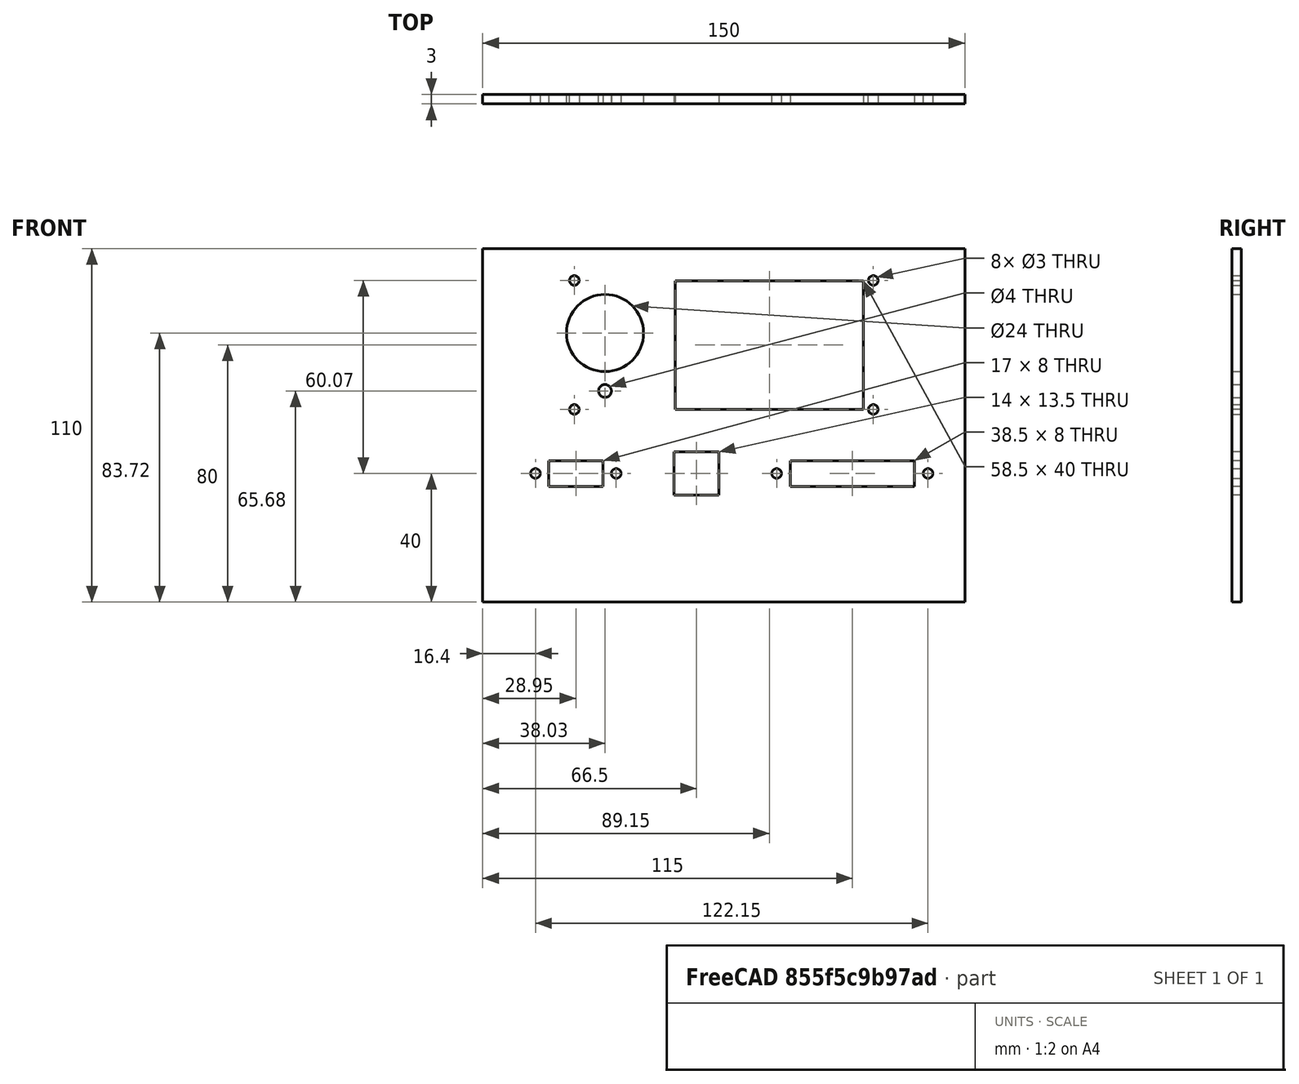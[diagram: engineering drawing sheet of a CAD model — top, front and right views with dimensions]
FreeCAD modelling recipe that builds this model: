
FCSTD DOCUMENT  (FreeCAD 0.19R24291 (Git))
Label: MountMini12864
License: All rights reserved
LicenseURL: http://en.wikipedia.org/wiki/All_rights_reserved
objects: TechDraw::DrawViewDimension×26, Sketcher::SketchObject×4, PartDesign::Pocket×2, PartDesign::Pad×1, Spreadsheet::Sheet×1, TechDraw::DrawSVGTemplate×1, PartDesign::Body×1, App::Part×1, TechDraw::DrawViewPart×1, TechDraw::DrawPage×1
note: 11 computed .brp shape members not serialized (recipe doc carries the construction recipe); baked Part::Feature solids carry a one-line shape summary decoded from their .brp

FEATURE [Sketcher::SketchObject] Sketch
  FullyConstrained = true
  MapMode = 5
  Placement = pos=(0,0,0) rot=(1,0,0;1.5708rad)
  Support = -> [XZ_Plane001]
  expr: Constraints[10] = <<Spreadsheet>>.Height
  expr: Constraints[9] = <<Spreadsheet>>.Width
  expr: Constraints[11] = <<Spreadsheet>>.OffsetVert
  expr: Constraints[12] = <<Spreadsheet>>.OffsetHorz
  sketch-geometry (5):
    g0: LineSegment StartX=-55 StartY=45 StartZ=0 EndX=95 EndY=45 EndZ=0
    g1: LineSegment StartX=95 StartY=45 StartZ=0 EndX=95 EndY=-65 EndZ=0
    g2: LineSegment StartX=95 StartY=-65 StartZ=0 EndX=-55 EndY=-65 EndZ=0
    g3: LineSegment StartX=-55 StartY=-65 StartZ=0 EndX=-55 EndY=45 EndZ=0
    g4: GeomPoint X=20 Y=-10 Z=0
  constraints (13):
    c: Coincident(g0,g1)
    c: Coincident(g1,g2)
    c: Coincident(g2,g3)
    c: Coincident(g3,g0)
    c: Horizontal(g0)
    c: Horizontal(g2)
    c: Vertical(g1)
    c: Vertical(g3)
    c: Symmetric(g0,g1,g4)
    c: DistanceX(g0,g0) = 150
    c: DistanceY(g3,g3) = 110
    c: DistanceY(g4,g-1) = 10
    c: DistanceX(g-1,g4) = 20
FEATURE [PartDesign::Pad] Pad  label="Pad Body"
  Direction = (1,1,1)
  Length = 3
  Length2 = 100
  Placement = pos=(0,0,0) rot=(1,0,0;1.5708rad)
  Profile = -> Sketch
  Type = 0
  expr: Length = <<Spreadsheet>>.Depth
FEATURE [Spreadsheet::Sheet] Spreadsheet
  cells = A1=MountMini12864; A2=Place a center point. Locate that point at Horz and Vertical Offset; A3=Place a rectangle around the point. ; A4=Select upper left corner, lower right cornder and center point. Set symetery; A5=Set Width to Width parameter (below), Set Height to Height Parameter below.; A6=Close the now fully parameterized and constrinaed sketch.; A7=Pad the sketch to the Depth prameter (below).; A9=Body; A10=OffsetHorz; B10(OffsetHorz)==20mm; A11=OffsetVert; B11(OffsetVert)==10mm; A13=Width; B13(Width)==150mm; C13=PCB is 189mm; A14=Height; B14(Height)==110mm; A15=Depth; B15(Depth)==3mm; A18=DisplayMount; A19=OffsetMountHorz; B19(OffsetMountHorz)==20mm; C19=Toward left; A20=OffsetMountVert; B20(OffsetMountVert)==15mm; C21=From drawing; A22=DisplayMountWidth; B22(DisplayMountWidth)==C22; C22==101.99 - 8.99; A23=DisplayMountHeight; B23(DisplayMountHeight)==C23; C23==44 - 3.86; A24=DisplayMountHoleDiameter; B24(DisplayMountHoleDiameter)==3mm; A26=OffsetDisplayHorz; B26(OffsetDisplayHorz)==61.6mm; C26=From edge; D26==70.59 - 8.99; A27=OffsetDisplayVert; B27(OffsetDisplayVert)==15mm; C27=From drawing; A28=DisplayWidth; B28(DisplayWidth)==58.5mm; C28==70.59 - 12.39; A29=DisplayHeight; B29(DisplayHeight)==40mm; C29==38.8mm; A31=OffsetEncoderHorz; B31(OffsetEncoderHorz)==12.53 - 3; C31=Guess; A32=OffserEncoderVert; B32(OffserEncoderVert)==(32.71 + 20.87) / 2 - 3; C32=Up from Mount; A33=EncoderDiameter; B33(EncoderDiameter)==24mm; C33=Measured Knob; A35=OffsetResetHorz; B35(OffsetResetHorz)==B31; C35=same as encoder; A36=OffserResetVert; B36(OffserResetVert)==5.75mm; C36=Up from Mount; A37=ResetDiameter; B37(ResetDiameter)==4mm; A40=DB25 Mount; A41=OffsetDB25MountHorz; B41(OffsetDB25MountHorz)==60mm; C41=This moves DB25, RJ12, and DB9; A42=OffsetDB25MountVert; B42(OffsetDB25MountVert)==25mm; C42=Down from center; A44=DB25MountWidth; B44(DB25MountWidth)==38.5mm; A45=DB25MountHeight; B45(DB25MountHeight)==8mm; A46=DB25MountHoleSpace; B46(DB25MountHoleSpace)==47.1mm; A47=DB25MountHoleDiameter; B47(DB25MountHoleDiameter)==3mm; A50=RJ12 Connector; A51=OffsetRJ12MountHorz; B51(OffsetRJ12MountHorz)==48.5mm; C51=From DB25; A52=OffsetRJ12MountVert; B52(OffsetRJ12MountVert)==25mm; A54=RJ12Width; B54(RJ12Width)==14mm; C54=13.5 mm measured; A55=RJ12Height; B55(RJ12Height)==13.5mm; C55=12.5 mm measured; A58=DB9 Mount; A59=OffsetDB9MountHorz; B59(OffsetDB9MountHorz)==86.05mm; A60=OffsetDB9MountVert; B60(OffsetDB9MountVert)==25mm; C60=Down from center; A62=DB9MountWidth; B62(DB9MountWidth)=17; C62==16.3mm; A63=DB9MountHeight; B63(DB9MountHeight)==8mm; A64=DB9MountHoleSpace; B64(DB9MountHoleSpace)==25.1mm; A65=DB9MountHoleDiameter; B65(DB9MountHoleDiameter)==3mm
FEATURE [Sketcher::SketchObject] Sketch001
  FullyConstrained = true
  MapMode = 5
  Placement = pos=(0,0,0) rot=(-1,0,0;1.5708rad)
  Support = -> [Pad]
  expr: Constraints[39] = <<Spreadsheet>>.OffsetMountHorz
  expr: Constraints[38] = <<Spreadsheet>>.OffsetEncoderHorz
  expr: Constraints[29] = <<Spreadsheet>>.DisplayWidth
  expr: Constraints[32] = <<Spreadsheet>>.OffsetDisplayHorz
  expr: Constraints[37] = <<Spreadsheet>>.OffserEncoderVert
  expr: Constraints[36] = <<Spreadsheet>>.OffserResetVert
  expr: Constraints[34] = <<Spreadsheet>>.ResetDiameter
  expr: Constraints[18] = <<Spreadsheet>>.DisplayMountHeight
  expr: Constraints[30] = <<Spreadsheet>>.DisplayHeight
  expr: Constraints[19] = <<Spreadsheet>>.OffsetMountVert
  expr: Constraints[33] = <<Spreadsheet>>.EncoderDiameter
  expr: Constraints[17] = <<Spreadsheet>>.DisplayMountWidth
  expr: Constraints[12] = <<Spreadsheet>>.DisplayMountHoleDiameter
  sketch-geometry (16):
    g0: LineSegment StartX=-26.5 StartY=5.07 StartZ=0 EndX=66.5 EndY=5.07 EndZ=0
    g1: LineSegment StartX=66.5 StartY=5.07 StartZ=0 EndX=66.5 EndY=-35.07 EndZ=0
    g2: LineSegment StartX=66.5 StartY=-35.07 StartZ=0 EndX=-26.5 EndY=-35.07 EndZ=0
    g3: LineSegment StartX=-26.5 StartY=-35.07 StartZ=0 EndX=-26.5 EndY=5.07 EndZ=0
    g4: GeomPoint X=20 Y=-15 Z=0
    g5: Circle CenterX=-26.5 CenterY=5.07 CenterZ=0 NormalX=0 NormalY=0 NormalZ=1 AngleXU=0 Radius=1.5
    g6: Circle CenterX=-26.5 CenterY=-35.07 CenterZ=0 NormalX=0 NormalY=0 NormalZ=1 AngleXU=0 Radius=1.5
    g7: Circle CenterX=66.5 CenterY=-35.07 CenterZ=0 NormalX=0 NormalY=0 NormalZ=1 AngleXU=0 Radius=1.5
    g8: Circle CenterX=66.5 CenterY=5.07 CenterZ=0 NormalX=0 NormalY=0 NormalZ=1 AngleXU=0 Radius=1.5
    g9: LineSegment StartX=4.9 StartY=5 StartZ=0 EndX=63.4 EndY=5 EndZ=0
    g10: LineSegment StartX=63.4 StartY=5 StartZ=0 EndX=63.4 EndY=-35 EndZ=0
    g11: LineSegment StartX=63.4 StartY=-35 StartZ=0 EndX=4.9 EndY=-35 EndZ=0
    g12: LineSegment StartX=4.9 StartY=-35 StartZ=0 EndX=4.9 EndY=5 EndZ=0
    g13: GeomPoint X=34.15 Y=-15 Z=0
    g14: Circle CenterX=-16.97 CenterY=-18.72 CenterZ=0 NormalX=0 NormalY=0 NormalZ=1 AngleXU=0 Radius=12
    g15: Circle CenterX=-16.97 CenterY=-0.68 CenterZ=0 NormalX=0 NormalY=0 NormalZ=1 AngleXU=0 Radius=2
  constraints (40):
    c: Coincident(g0,g1)
    c: Coincident(g1,g2)
    c: Coincident(g2,g3)
    c: Coincident(g3,g0)
    c: Horizontal(g0)
    c: Horizontal(g2)
    c: Vertical(g1)
    c: Vertical(g3)
    c: Symmetric(g0,g1,g4)
    c: Equal(g8,g7)
    c: Equal(g7,g6)
    c: Equal(g6,g5)
    c: Diameter(g5) = 3
    c: Coincident(g5,g0)
    c: Coincident(g6,g2)
    c: Coincident(g7,g1)
    c: Coincident(g8,g0)
    c: DistanceX(g0,g0) = 93
    c: DistanceY(g3,g3) = 40.14
    c: DistanceY(g4,g-1) = 15
    c: Coincident(g9,g10)
    c: Coincident(g10,g11)
    c: Coincident(g11,g12)
    c: Coincident(g12,g9)
    c: Horizontal(g9)
    c: Horizontal(g11)
    c: Vertical(g10)
    c: Vertical(g12)
    c: Symmetric(g9,g10,g13)
    c: DistanceX(g9,g9) = 58.5
    c: DistanceY(g10,g10) = 40
    c: Horizontal(g13,g4)
    c: DistanceX(g9,g8) = 61.6
    c: Diameter(g14) = 24
    c: Diameter(g15) = 4
    c: Vertical(g14,g15)
    c: DistanceY(g15,g5) = 5.75
    c: DistanceY(g14,g5) = 23.79
    c: DistanceX(g5,g14) = 9.53
    c: DistanceX(g-1,g4) = 20
FEATURE [PartDesign::Pocket] Pocket  label="PocketDisplayMountHoles"
  BaseFeature = -> Pad
  Length = 5
  Length2 = 100
  Placement = pos=(0,0,0) rot=(1,0,0;1.5708rad)
  Profile = -> Sketch001
  Type = 1
FEATURE [Sketcher::SketchObject] Sketch002
  FullyConstrained = true
  MapMode = 5
  Placement = pos=(0,0,0) rot=(-1,0,0;1.5708rad)
  Support = -> [Pocket]
  expr: Constraints[48] = <<Spreadsheet>>.DB9MountHoleSpace
  expr: Constraints[45] = <<Spreadsheet>>.OffsetDB9MountHorz
  expr: Constraints[42] = <<Spreadsheet>>.DB9MountWidth
  expr: Constraints[30] = <<Spreadsheet>>.RJ12Height
  expr: Constraints[32] = <<Spreadsheet>>.OffsetRJ12MountHorz
  expr: Constraints[29] = <<Spreadsheet>>.RJ12Width
  expr: Constraints[19] = <<Spreadsheet>>.OffsetDB25MountHorz
  expr: Constraints[43] = <<Spreadsheet>>.DB9MountHeight
  expr: Constraints[18] = <<Spreadsheet>>.DB25MountHoleSpace
  expr: Constraints[14] = <<Spreadsheet>>.DB25MountHoleDiameter
  expr: Constraints[9] = <<Spreadsheet>>.DB25MountWidth
  expr: Constraints[11] = <<Spreadsheet>>.OffsetDB25MountVert
  expr: Constraints[10] = <<Spreadsheet>>.DB25MountHeight
  sketch-geometry (21):
    g0: LineSegment StartX=40.75 StartY=29 StartZ=0 EndX=79.25 EndY=29 EndZ=0
    g1: LineSegment StartX=79.25 StartY=29 StartZ=0 EndX=79.25 EndY=21 EndZ=0
    g2: LineSegment StartX=79.25 StartY=21 StartZ=0 EndX=40.75 EndY=21 EndZ=0
    g3: LineSegment StartX=40.75 StartY=21 StartZ=0 EndX=40.75 EndY=29 EndZ=0
    g4: GeomPoint X=60 Y=25 Z=0
    g5: LineSegment StartX=36.45 StartY=25 StartZ=0 EndX=83.55 EndY=25 EndZ=0
    g6: Circle CenterX=36.45 CenterY=25 CenterZ=0 NormalX=0 NormalY=0 NormalZ=1 AngleXU=0 Radius=1.5
    g7: Circle CenterX=83.55 CenterY=25 CenterZ=0 NormalX=0 NormalY=0 NormalZ=1 AngleXU=0 Radius=1.5
    g8: LineSegment StartX=4.5 StartY=31.75 StartZ=0 EndX=18.5 EndY=31.75 EndZ=0
    g9: LineSegment StartX=18.5 StartY=31.75 StartZ=0 EndX=18.5 EndY=18.25 EndZ=0
    g10: LineSegment StartX=18.5 StartY=18.25 StartZ=0 EndX=4.5 EndY=18.25 EndZ=0
    g11: LineSegment StartX=4.5 StartY=18.25 StartZ=0 EndX=4.5 EndY=31.75 EndZ=0
    g12: GeomPoint X=11.5 Y=25 Z=0
    g13: LineSegment StartX=-34.55 StartY=29 StartZ=0 EndX=-17.55 EndY=29 EndZ=0
    g14: LineSegment StartX=-17.55 StartY=29 StartZ=0 EndX=-17.55 EndY=21 EndZ=0
    g15: LineSegment StartX=-17.55 StartY=21 StartZ=0 EndX=-34.55 EndY=21 EndZ=0
    g16: LineSegment StartX=-34.55 StartY=21 StartZ=0 EndX=-34.55 EndY=29 EndZ=0
    g17: GeomPoint X=-26.05 Y=25 Z=0
    g18: LineSegment StartX=-38.6 StartY=25 StartZ=0 EndX=-13.5 EndY=25 EndZ=0
    g19: Circle CenterX=-38.6 CenterY=25 CenterZ=0 NormalX=0 NormalY=0 NormalZ=1 AngleXU=0 Radius=1.5
    g20: Circle CenterX=-13.5 CenterY=25 CenterZ=0 NormalX=0 NormalY=0 NormalZ=1 AngleXU=0 Radius=1.5
  constraints (53):
    c: Coincident(g0,g1)
    c: Coincident(g1,g2)
    c: Coincident(g2,g3)
    c: Coincident(g3,g0)
    c: Horizontal(g0)
    c: Horizontal(g2)
    c: Vertical(g1)
    c: Vertical(g3)
    c: Symmetric(g0,g1,g4)
    c: DistanceX(g0,g0) = 38.5
    c: DistanceY(g3,g3) = 8
    c: DistanceY(g-1,g4) = 25
    c: Horizontal(g5)
    c: Symmetric(g5,g5,g4)
    c: Diameter(g6) = 3
    c: Equal(g6,g7)
    c: Coincident(g7,g5)
    c: Coincident(g6,g5)
    c: DistanceX(g5,g5) = 47.1
    c: DistanceX(g-1,g4) = 60
    c: Coincident(g8,g9)
    c: Coincident(g9,g10)
    c: Coincident(g10,g11)
    c: Coincident(g11,g8)
    c: Horizontal(g8)
    c: Horizontal(g10)
    c: Vertical(g9)
    c: Vertical(g11)
    c: Symmetric(g8,g9,g12)
    c: DistanceX(g8,g8) = 14
    c: DistanceY(g11,g11) = 13.5
    c: Horizontal(g12,g4)
    c: DistanceX(g12,g4) = 48.5
    c: Coincident(g13,g14)
    c: Coincident(g14,g15)
    c: Coincident(g15,g16)
    c: Coincident(g16,g13)
    c: Horizontal(g13)
    c: Horizontal(g15)
    c: Vertical(g14)
    c: Vertical(g16)
    c: Symmetric(g13,g14,g17)
    c: DistanceX(g13,g13) = 17
    c: DistanceY(g14,g14) = 8
    c: Horizontal(g17,g4)
    c: DistanceX(g17,g4) = 86.05
    c: Horizontal(g18)
    c: Symmetric(g18,g18,g17)
    c: DistanceX(g18,g18) = 25.1
    c: Equal(g19,g20)
    c: Equal(g20,g6)
    c: Coincident(g20,g18)
    c: Coincident(g19,g18)
FEATURE [PartDesign::Pocket] Pocket001  label="PockeDB25Mount"
  BaseFeature = -> Pocket
  Length = 5
  Length2 = 100
  Placement = pos=(0,0,0) rot=(1,0,0;1.5708rad)
  Profile = -> Sketch002
  Type = 1
FEATURE [TechDraw::DrawSVGTemplate] Template
  EditableTexts = Approved1=Approved 1; Approved2=Approved 2; CheckedBy=Checked By; Code=Code; CompanyAddress=1234 Main St; CompanyName=Company Name; DrawingNumber=Drawing Number; DrawingTitle1=Drawing Title 1; DrawingTitle2=Drawing Title 2; DrawingTitle3=Drawing Title 3; DrawnBy=Drawn By; Revision=Rev; Scale=Scale; Sheet=Sheet n of m
  Height = 215.9
  Orientation = 1
  Width = 279.4
FEATURE [Sketcher::SketchObject] Sketch003
  FullyConstrained = false
  MapMode = 5
  Placement = pos=(0,0,0) rot=(-1,0,0;1.5708rad)
  Support = -> [Pocket001]
  sketch-geometry (4):
    g0: Circle CenterX=12.7 CenterY=-2.5731 CenterZ=0 NormalX=0 NormalY=0 NormalZ=1 AngleXU=0 Radius=2.5
    g1: Circle CenterX=16.5168 CenterY=-30.4911 CenterZ=0 NormalX=0 NormalY=0 NormalZ=1 AngleXU=0 Radius=2.5
    g2: Circle CenterX=56.321 CenterY=-7.59722 CenterZ=0 NormalX=0 NormalY=0 NormalZ=1 AngleXU=0 Radius=2.5
    g3: Circle CenterX=54.5057 CenterY=-28.5407 CenterZ=0 NormalX=0 NormalY=0 NormalZ=1 AngleXU=0 Radius=2.5
  constraints (4):
    c: Diameter(g0) = 5
    c: Equal(g0,g1)
    c: Equal(g1,g2)
    c: Equal(g2,g3)
FEATURE [PartDesign::Body] Body  label="Body_MountMini12864"
  Group = -> [Sketch,Pad,Sketch001,Pocket,Sketch003,Sketch002,Pocket001]
  Origin = -> Origin001
  Tip = -> Pocket001
FEATURE [App::Part] Part  label="Part_MountMini12864"
  Group = -> [Body]
  Origin = -> Origin
FEATURE [TechDraw::DrawViewPart] View
  CoarseView = false
  Direction = (0,1,0)
  Focus = 100
  HardHidden = false
  IsoCount = 0
  IsoHidden = false
  IsoVisible = false
  LockPosition = false
  Perspective = false
  Rotation = 0
  ScaleType = 2
  SeamHidden = false
  SeamVisible = true
  SmoothHidden = false
  SmoothVisible = true
  Source = -> [Part]
  X = 141.69
  XDirection = (-1,0,0)
  Y = 136.14
FEATURE [TechDraw::DrawViewDimension] Dimension
  Arbitrary = false
  ArbitraryTolerances = false
  EqualTolerance = true
  FormatSpec = %.3f
  FormatSpecOverTolerance = %+.3f
  FormatSpecUnderTolerance = %+.3f
  Inverted = false
  LockPosition = false
  MeasureType = 1
  OverTolerance = 0
  References2D = -> [View]
  Rotation = 0
  ScaleType = 2
  TheoreticalExact = false
  Type = 1
  UnderTolerance = 0
  X = -46.9351
  Y = 26.2363
FEATURE [TechDraw::DrawViewDimension] Dimension001
  Arbitrary = false
  ArbitraryTolerances = false
  EqualTolerance = true
  FormatSpec = %.3f
  FormatSpecOverTolerance = %+.3f
  FormatSpecUnderTolerance = %+.3f
  Inverted = false
  LockPosition = false
  MeasureType = 1
  OverTolerance = 0
  References2D = -> [View]
  Rotation = 0
  ScaleType = 2
  TheoreticalExact = false
  Type = 2
  UnderTolerance = 0
  X = -27.358
  Y = 7.38784
FEATURE [TechDraw::DrawViewDimension] Dimension002
  Arbitrary = false
  ArbitraryTolerances = false
  EqualTolerance = true
  FormatSpec = %.3f
  FormatSpecOverTolerance = %+.3f
  FormatSpecUnderTolerance = %+.3f
  Inverted = false
  LockPosition = false
  MeasureType = 1
  OverTolerance = 0
  References2D = -> [View]
  Rotation = 0
  ScaleType = 2
  TheoreticalExact = false
  Type = 1
  UnderTolerance = 0
  X = 0
  Y = -63.952
FEATURE [TechDraw::DrawViewDimension] Dimension003
  Arbitrary = false
  ArbitraryTolerances = false
  EqualTolerance = true
  FormatSpec = %.3f
  FormatSpecOverTolerance = %+.3f
  FormatSpecUnderTolerance = %+.3f
  Inverted = false
  LockPosition = false
  MeasureType = 1
  OverTolerance = 0
  References2D = -> [View]
  Rotation = 0
  ScaleType = 2
  TheoreticalExact = false
  Type = 2
  UnderTolerance = 0
  X = 94.5
  Y = 0
FEATURE [TechDraw::DrawViewDimension] Dimension004
  Arbitrary = false
  ArbitraryTolerances = false
  EqualTolerance = true
  FormatSpec = ⌀%.3f
  FormatSpecOverTolerance = %+.3f
  FormatSpecUnderTolerance = %+.3f
  Inverted = false
  LockPosition = false
  MeasureType = 1
  OverTolerance = 0
  References2D = -> [View]
  Rotation = 0
  ScaleType = 2
  TheoreticalExact = false
  Type = 5
  UnderTolerance = 0
  X = 36.8493
  Y = 30.4007
FEATURE [TechDraw::DrawViewDimension] Dimension005
  Arbitrary = false
  ArbitraryTolerances = false
  EqualTolerance = true
  FormatSpec = ⌀%.3f
  FormatSpecOverTolerance = %+.3f
  FormatSpecUnderTolerance = %+.3f
  Inverted = false
  LockPosition = false
  MeasureType = 1
  OverTolerance = 0
  References2D = -> [View]
  Rotation = 0
  ScaleType = 2
  TheoreticalExact = false
  Type = 5
  UnderTolerance = 0
  X = 36.8493
  Y = 11.5154
FEATURE [TechDraw::DrawViewDimension] Dimension006
  Arbitrary = false
  ArbitraryTolerances = false
  EqualTolerance = true
  FormatSpec = ⌀%.3f
  FormatSpecOverTolerance = %+.3f
  FormatSpecUnderTolerance = %+.3f
  Inverted = false
  LockPosition = false
  MeasureType = 1
  OverTolerance = 0
  References2D = -> [View]
  Rotation = 0
  ScaleType = 2
  TheoreticalExact = false
  Type = 5
  UnderTolerance = 0
  X = 36.8493
  Y = 2.07277
FEATURE [TechDraw::DrawViewDimension] Dimension007
  Arbitrary = false
  ArbitraryTolerances = false
  EqualTolerance = true
  FormatSpec = %.3f
  FormatSpecOverTolerance = %+.3f
  FormatSpecUnderTolerance = %+.3f
  Inverted = false
  LockPosition = false
  MeasureType = 1
  OverTolerance = 0
  References2D = -> [View]
  Rotation = 0
  ScaleType = 2
  TheoreticalExact = false
  Type = 1
  UnderTolerance = 0
  X = -20.6064
  Y = 50.0465
FEATURE [TechDraw::DrawViewDimension] Dimension009
  Arbitrary = false
  ArbitraryTolerances = false
  EqualTolerance = true
  FormatSpec = %.3f
  FormatSpecOverTolerance = %+.3f
  FormatSpecUnderTolerance = %+.3f
  Inverted = false
  LockPosition = false
  MeasureType = 1
  OverTolerance = 0
  References2D = -> [View]
  Rotation = 0
  ScaleType = 2
  TheoreticalExact = false
  Type = 1
  UnderTolerance = 0
  X = -60.5788
  Y = -12.8057
FEATURE [TechDraw::DrawViewDimension] Dimension010
  Arbitrary = false
  ArbitraryTolerances = false
  EqualTolerance = true
  FormatSpec = %.3f
  FormatSpecOverTolerance = %+.3f
  FormatSpecUnderTolerance = %+.3f
  Inverted = false
  LockPosition = false
  MeasureType = 1
  OverTolerance = 0
  References2D = -> [View]
  Rotation = 0
  ScaleType = 2
  TheoreticalExact = false
  Type = 1
  UnderTolerance = 0
  X = -62.4212
  Y = -18.7089
FEATURE [TechDraw::DrawViewDimension] Dimension011
  Arbitrary = false
  ArbitraryTolerances = false
  EqualTolerance = true
  FormatSpec = %.3f
  FormatSpecOverTolerance = %+.3f
  FormatSpecUnderTolerance = %+.3f
  Inverted = false
  LockPosition = false
  MeasureType = 1
  OverTolerance = 0
  References2D = -> [View]
  Rotation = 0
  ScaleType = 2
  TheoreticalExact = false
  Type = 2
  UnderTolerance = 0
  X = 42.4926
  Y = -21.7877
FEATURE [TechDraw::DrawViewDimension] Dimension012
  Arbitrary = false
  ArbitraryTolerances = false
  EqualTolerance = true
  FormatSpec = %.3f
  FormatSpecOverTolerance = %+.3f
  FormatSpecUnderTolerance = %+.3f
  Inverted = false
  LockPosition = false
  MeasureType = 1
  OverTolerance = 0
  References2D = -> [View]
  Rotation = 0
  ScaleType = 2
  TheoreticalExact = false
  Type = 1
  UnderTolerance = 0
  X = 21.7863
  Y = -19.3998
FEATURE [TechDraw::DrawViewDimension] Dimension013
  Arbitrary = false
  ArbitraryTolerances = false
  EqualTolerance = true
  FormatSpec = %.3f
  FormatSpecOverTolerance = %+.3f
  FormatSpecUnderTolerance = %+.3f
  Inverted = false
  LockPosition = false
  MeasureType = 1
  OverTolerance = 0
  References2D = -> [View]
  Rotation = 0
  ScaleType = 2
  TheoreticalExact = false
  Type = 1
  UnderTolerance = 0
  X = 22.7075
  Y = -13.7269
FEATURE [TechDraw::DrawViewDimension] Dimension014
  Arbitrary = false
  ArbitraryTolerances = false
  EqualTolerance = true
  FormatSpec = %.3f
  FormatSpecOverTolerance = %+.3f
  FormatSpecUnderTolerance = %+.3f
  Inverted = false
  LockPosition = false
  MeasureType = 1
  OverTolerance = 0
  References2D = -> [View]
  Rotation = 0
  ScaleType = 2
  TheoreticalExact = false
  Type = 1
  UnderTolerance = 0
  X = -19.2183
  Y = -15.9589
FEATURE [TechDraw::DrawViewDimension] Dimension015
  Arbitrary = false
  ArbitraryTolerances = false
  EqualTolerance = true
  FormatSpec = %.3f
  FormatSpecOverTolerance = %+.3f
  FormatSpecUnderTolerance = %+.3f
  Inverted = false
  LockPosition = false
  MeasureType = 1
  OverTolerance = 0
  References2D = -> [View]
  Rotation = 0
  ScaleType = 2
  TheoreticalExact = false
  Type = 2
  UnderTolerance = 0
  X = -4.15754
  Y = -22.9392
FEATURE [TechDraw::DrawViewDimension] Dimension016
  Arbitrary = false
  ArbitraryTolerances = false
  EqualTolerance = true
  FormatSpec = %.3f
  FormatSpecOverTolerance = %+.3f
  FormatSpecUnderTolerance = %+.3f
  Inverted = false
  LockPosition = false
  MeasureType = 1
  OverTolerance = 0
  References2D = -> [View]
  Rotation = 0
  ScaleType = 2
  TheoreticalExact = false
  Type = 1
  UnderTolerance = 0
  X = -86.2432
  Y = -40.494
FEATURE [TechDraw::DrawViewDimension] Dimension017
  Arbitrary = false
  ArbitraryTolerances = false
  EqualTolerance = true
  FormatSpec = %.3f
  FormatSpecOverTolerance = %+.3f
  FormatSpecUnderTolerance = %+.3f
  Inverted = false
  LockPosition = false
  MeasureType = 1
  OverTolerance = 0
  References2D = -> [View]
  Rotation = 0
  ScaleType = 2
  TheoreticalExact = false
  Type = 1
  UnderTolerance = 0
  X = -55.1275
  Y = -6.2187
FEATURE [TechDraw::DrawViewDimension] Dimension018
  Arbitrary = false
  ArbitraryTolerances = false
  EqualTolerance = true
  FormatSpec = %.3f
  FormatSpecOverTolerance = %+.3f
  FormatSpecUnderTolerance = %+.3f
  Inverted = false
  LockPosition = false
  MeasureType = 1
  OverTolerance = 0
  References2D = -> [View]
  Rotation = 0
  ScaleType = 2
  TheoreticalExact = false
  Type = 1
  UnderTolerance = 0
  X = -38.0735
  Y = -55.464
FEATURE [TechDraw::DrawViewDimension] Dimension019
  Arbitrary = false
  ArbitraryTolerances = false
  EqualTolerance = true
  FormatSpec = %.3f
  FormatSpecOverTolerance = %+.3f
  FormatSpecUnderTolerance = %+.3f
  Inverted = false
  LockPosition = false
  MeasureType = 1
  OverTolerance = 0
  References2D = -> [View]
  Rotation = 0
  ScaleType = 2
  TheoreticalExact = false
  Type = 2
  UnderTolerance = 0
  X = 51.9089
  Y = -34.0732
FEATURE [TechDraw::DrawViewDimension] Dimension020
  Arbitrary = false
  ArbitraryTolerances = false
  EqualTolerance = true
  FormatSpec = %.3f
  FormatSpecOverTolerance = %+.3f
  FormatSpecUnderTolerance = %+.3f
  Inverted = false
  LockPosition = false
  MeasureType = 1
  OverTolerance = 0
  References2D = -> [View]
  Rotation = 0
  ScaleType = 2
  TheoreticalExact = false
  Type = 2
  UnderTolerance = 0
  X = -37.2132
  Y = -25.7474
FEATURE [TechDraw::DrawViewDimension] Dimension021
  Arbitrary = false
  ArbitraryTolerances = false
  EqualTolerance = true
  FormatSpec = %.3f
  FormatSpecOverTolerance = %+.3f
  FormatSpecUnderTolerance = %+.3f
  Inverted = false
  LockPosition = false
  MeasureType = 1
  OverTolerance = 0
  References2D = -> [View]
  Rotation = 0
  ScaleType = 2
  TheoreticalExact = false
  Type = 1
  UnderTolerance = 0
  X = -34.0152
  Y = 62.7763
FEATURE [TechDraw::DrawViewDimension] Dimension022
  Arbitrary = false
  ArbitraryTolerances = false
  EqualTolerance = true
  FormatSpec = %.3f
  FormatSpecOverTolerance = %+.3f
  FormatSpecUnderTolerance = %+.3f
  Inverted = false
  LockPosition = false
  MeasureType = 1
  OverTolerance = 0
  References2D = -> [View]
  Rotation = 0
  ScaleType = 2
  TheoreticalExact = false
  Type = 1
  UnderTolerance = 0
  X = -85.4324
  Y = 49.9656
FEATURE [TechDraw::DrawViewDimension] Dimension023
  Arbitrary = false
  ArbitraryTolerances = false
  EqualTolerance = true
  FormatSpec = %.3f
  FormatSpecOverTolerance = %+.3f
  FormatSpecUnderTolerance = %+.3f
  Inverted = false
  LockPosition = false
  MeasureType = 1
  OverTolerance = 0
  References2D = -> [View]
  Rotation = 0
  ScaleType = 2
  TheoreticalExact = false
  Type = 2
  UnderTolerance = 0
  X = 60.591
  Y = -21.7507
FEATURE [TechDraw::DrawViewDimension] Dimension024
  Arbitrary = false
  ArbitraryTolerances = false
  EqualTolerance = true
  FormatSpec = %.3f
  FormatSpecOverTolerance = %+.3f
  FormatSpecUnderTolerance = %+.3f
  Inverted = false
  LockPosition = false
  MeasureType = 1
  OverTolerance = 0
  References2D = -> [View]
  Rotation = 0
  ScaleType = 2
  TheoreticalExact = false
  Type = 2
  UnderTolerance = 0
  X = -105.63
  Y = -25.5
FEATURE [TechDraw::DrawViewDimension] Dimension025
  Arbitrary = false
  ArbitraryTolerances = false
  EqualTolerance = true
  FormatSpec = %.3f
  FormatSpecOverTolerance = %+.3f
  FormatSpecUnderTolerance = %+.3f
  Inverted = false
  LockPosition = false
  MeasureType = 1
  OverTolerance = 0
  References2D = -> [View]
  Rotation = 0
  ScaleType = 2
  TheoreticalExact = false
  Type = 1
  UnderTolerance = 0
  X = -83.3792
  Y = 3.93382
FEATURE [TechDraw::DrawViewDimension] Dimension026
  Arbitrary = false
  ArbitraryTolerances = false
  EqualTolerance = true
  FormatSpec = %.3f
  FormatSpecOverTolerance = %+.3f
  FormatSpecUnderTolerance = %+.3f
  Inverted = false
  LockPosition = false
  MeasureType = 1
  OverTolerance = 0
  References2D = -> [View]
  Rotation = 0
  ScaleType = 2
  TheoreticalExact = false
  Type = 1
  UnderTolerance = 0
  X = -89.9939
  Y = -75.7733
FEATURE [TechDraw::DrawPage] Page
  KeepUpdated = true
  NextBalloonIndex = 1
  ProjectionType = 0
  Template = -> Template
  Views = -> [View,Dimension,Dimension001,Dimension002,Dimension003,Dimension004,Dimension005,Dimension006,Dimension007,Dimension009,Dimension010,Dimension011,Dimension012,Dimension013,Dimension014,Dimension015,Dimension016,Dimension017,Dimension018,Dimension019,Dimension020,Dimension021,Dimension022,Dimension023,Dimension024,Dimension025,Dimension026]
